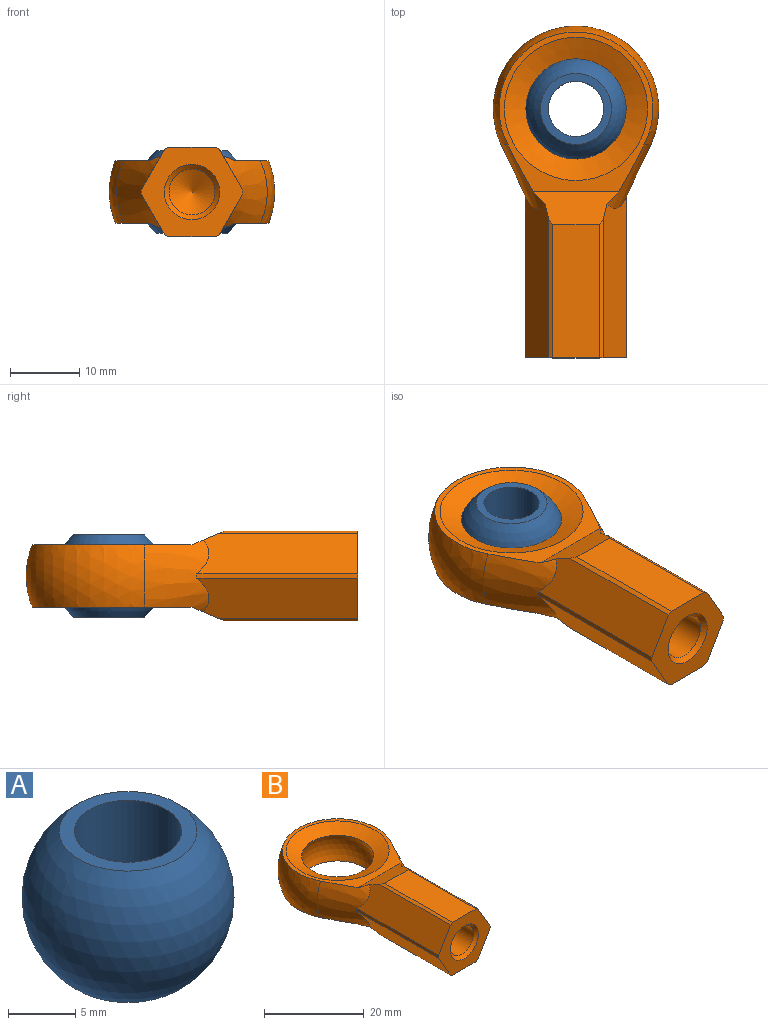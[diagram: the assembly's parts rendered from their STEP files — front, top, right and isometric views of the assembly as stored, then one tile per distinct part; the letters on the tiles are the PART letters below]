
ASSEMBLY  parts=2 mates=1
PART A: 4 faces, bbox 15.8x15.8x12 mm
  f0: plane 10.28x10.28mm, normal (0,0,1), area 32.7mm2, adj f1,f3
  f1: cylinder r=4mm len=12mm, axis (0,0,-1), area 301.6mm2, adj f0,f2
  f2: plane 10.28x10.28mm, normal (0,0,-1), area 32.7mm2, adj f1,f3
  f3: sphere r=7.9mm, area 595.6mm2, adj f0,f2
PART B: 26 faces, bbox 24.1x48.1x24.1 mm
  f0: plane 23.28x5.79mm, normal (-0.87,0,-0.5), area 146.4mm2, adj f9,f10,f13,f15,f17
  f1: plane 23.28x5.79mm, normal (-0.87,0,0.5), area 146.4mm2, adj f2,f10,f13,f15,f18
  f2: cylinder r=7.31mm len=20.12mm, axis (0,-1,0), area 13.9mm2, adj f1,f3,f15,f18
  f3: plane 19.29x6.69mm, normal (0,0,1), area 129mm2, adj f2,f4,f15,f18
  f4: cylinder r=7.31mm len=20.12mm, axis (0,-1,0), area 13.9mm2, adj f3,f5,f15,f18
  f5: plane 23.28x5.79mm, normal (0.87,0,0.5), area 146.4mm2, adj f4,f11,f14,f15,f18
  f6: plane 23.28x5.79mm, normal (0.87,0,-0.5), area 146.4mm2, adj f7,f11,f14,f15,f17
  f7: cylinder r=7.31mm len=20.12mm, axis (0,-1,0), area 13.9mm2, adj f6,f8,f15,f17
  f8: plane 19.29x6.69mm, normal (0,0,-1), area 129mm2, adj f7,f9,f15,f17
  f9: cylinder r=7.31mm len=20.12mm, axis (0,-1,0), area 13.9mm2, adj f0,f8,f15,f17
  f10: cone r=10.88mm half-angle=25deg, axis (0,1,0), area 95.3mm2, adj f0,f1,f12,f13,f16,f17,f18,f19
  f11: cone r=10.88mm half-angle=25deg, axis (0,1,0), area 95.3mm2, adj f5,f6,f12,f14,f16,f17,f18,f19
  f12: sphere r=12mm, area 436.1mm2, adj f10,f11,f16,f19
  f13: cylinder r=7.31mm len=23.28mm, axis (0,-1,0), area 16.5mm2, adj f0,f1,f10,f15
  f14: cylinder r=7.31mm len=23.28mm, axis (0,-1,0), area 16.5mm2, adj f5,f6,f11,f15
  f15: plane 14.62x13mm, normal (0,-1,0), area 95.7mm2, adj f0,f1,f2,f3,f4,f5,f6,f7
  f16: plane 23.13x22.25mm, normal (0,0,-1), area 78.6mm2, adj f10,f11,f12,f17,f25
  f17: plane 12.49x4.84mm, normal (0,0.39,-0.92), area 46.4mm2, adj f0,f6,f7,f8,f9,f10,f11,f16
  f18: plane 12.49x4.84mm, normal (0,0.39,0.92), area 46.4mm2, adj f1,f2,f3,f4,f5,f10,f11,f19
  f19: plane 23.13x22.25mm, normal (0,0,1), area 78.6mm2, adj f10,f11,f12,f18,f23
  f20: cone r=0mm half-angle=60deg, axis (0,-1,0), area 40.1mm2, adj f21
  f21: cylinder r=3.32mm len=16.32mm, axis (0,-1,0), area 340.9mm2, adj f20,f22
  f22: cone r=3.32mm half-angle=45deg, axis (0,-1,0), area 22mm2, adj f15,f21
  f23: cone r=10.35mm half-angle=66.5deg, axis (0,0,1), area 187.2mm2, adj f19,f24
  f24: sphere r=7.9mm, area 312.7mm2, adj f23,f25
  f25: cone r=7.24mm half-angle=66.5deg, axis (0,0,-1), area 187.2mm2, adj f16,f24
PLACE A rot(axis=(1,0,0),180deg) t=(-3.03,35.49,-9.9)mm
PLACE B t=(-3.03,-0.51,-9.9)mm
MATE ball A.f1 <-> B.f23  axis (0,0,-1) through (-3.03,35.49,-9.9)mm
